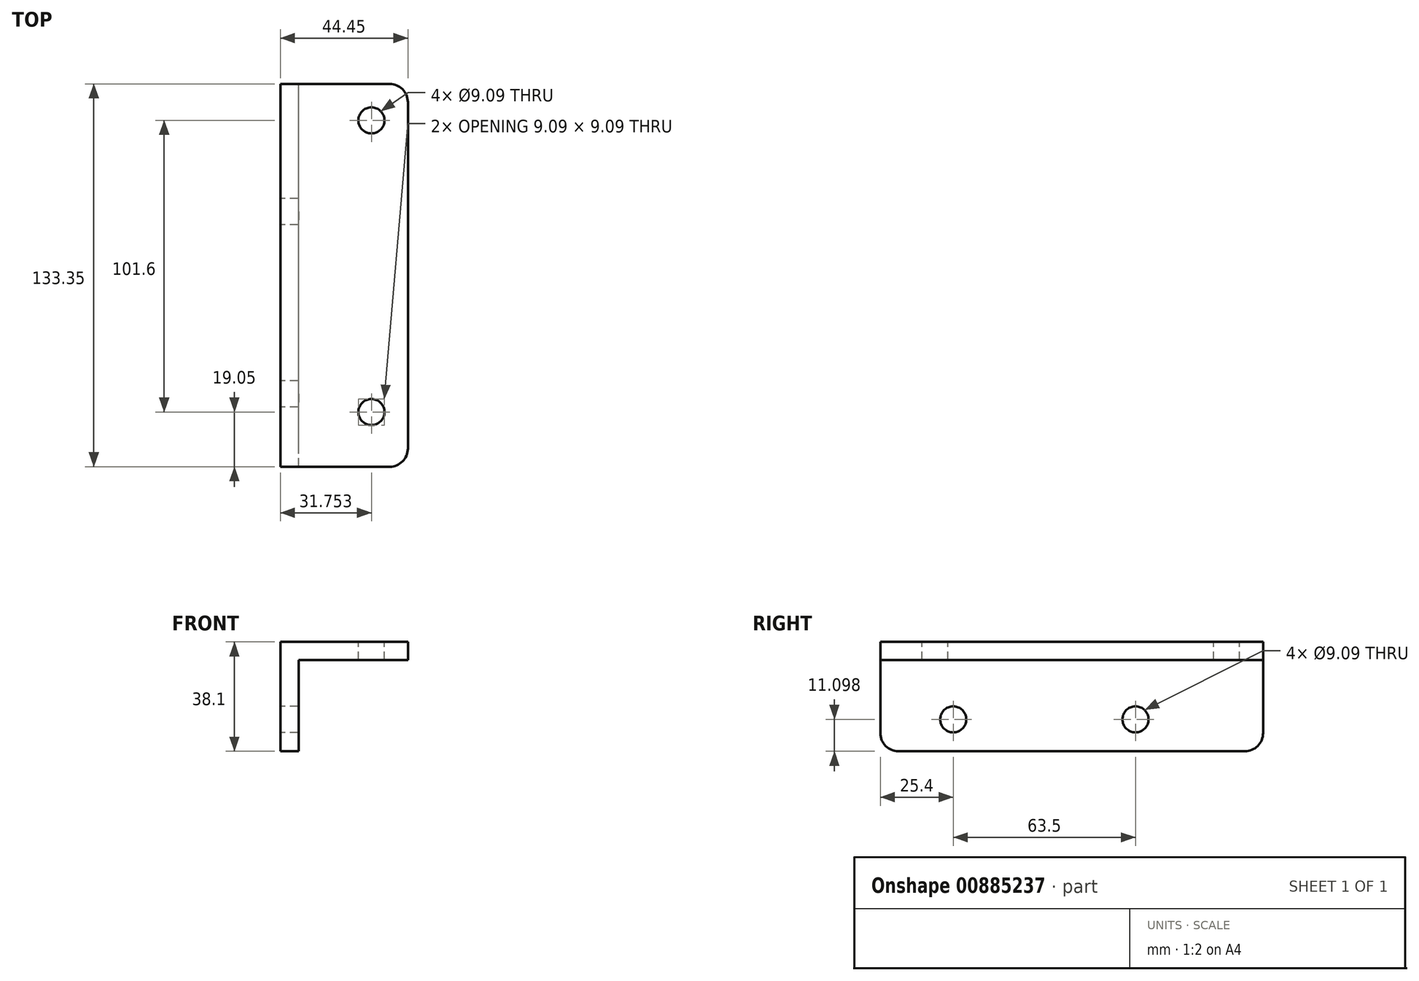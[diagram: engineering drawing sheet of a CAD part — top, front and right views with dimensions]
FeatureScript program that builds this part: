
annotation { "Feature Type Name" : "Feature", "Feature Type Description" : "" }
export const myFeature = defineFeature(function(context is Context, id is Id, definition is map)
    precondition{}
    {
        {
            var Q0;
            Q0=qCreatedBy(makeId("Front.planeOp"),FACE);
            var sketch = newSketch(context, id + "F0", { "sketchPlane" : qUnion([Q0])});
            skLineSegment(sketch, "E0", {"start": v(-40.8, -11.58) * mm, "end": v(-40.8, 26.52) * mm});
            skLineSegment(sketch, "E1", {"start": v(-40.8, 26.52) * mm, "end": v(3.65, 26.52) * mm});
            skLineSegment(sketch, "E2", {"start": v(3.65, 26.52) * mm, "end": v(3.65, 20.17) * mm});
            skLineSegment(sketch, "E3", {"start": v(3.65, 20.17) * mm, "end": v(-34.45, 20.17) * mm});
            skLineSegment(sketch, "E4", {"start": v(-34.45, 20.17) * mm, "end": v(-34.45, -11.58) * mm});
            skLineSegment(sketch, "E5", {"start": v(-34.45, -11.58) * mm, "end": v(-40.8, -11.58) * mm});
            skSolve(sketch);
        }
        {
            var Q0;
            Q0=makeQuery(id+"F0.imprint","IMPRINT",FACE,{"disambiguationData":[TD([[makeQuery(id+"F0.imprint","IMPRINT",EDGE,{"derivedFrom":sQuery(id+"F0.wireOp",EDGE,"E0")}),-1.0]])]});
            extrude(context, id + "F1", {"entities" : qUnion([Q0]), "depth" : 133.35 * mm, "offsetDistance" : 25.4 * mm});
        }
        {
            var Q0;
            Q0=makeQuery(id+"F1.opExtrude","SWEPT_FACE",FACE,{"disambiguationData":[OSD([sQuery(id+"F0.wireOp",EDGE,"E0")])]});
            var sketch = newSketch(context, id + "F2", { "sketchPlane" : qUnion([Q0])});
            skLineSegment(sketch, "E6", {"start": v(133.35, 26.52) * mm, "end": v(133.35, -0.48) * mm, "construction": true});
            skLineSegment(sketch, "E7", {"start": v(133.35, -0.48) * mm, "end": v(107.95, -0.48) * mm, "construction": true});
            skLineSegment(sketch, "E8", {"start": v(107.95, -0.48) * mm, "end": v(44.45, -0.48) * mm, "construction": true});
            skCircle(sketch, "E9", {"center": v(107.95, -0.48) * mm, "radius": 4.55 * mm});
            skCircle(sketch, "E10", {"center": v(44.45, -0.48) * mm, "radius": 4.55 * mm});
            skSolve(sketch);
        }
        {
            var Q0;
            Q0=makeQuery(id+"F2.imprint","IMPRINT",FACE,{"disambiguationData":[TD([[makeQuery(id+"F2.imprint","IMPRINT",EDGE,{"derivedFrom":sQuery(id+"F2.wireOp",EDGE,"E9")}),1.0]])]});
            var Q1;
            Q1=makeQuery(id+"F2.imprint","IMPRINT",FACE,{"disambiguationData":[TD([[makeQuery(id+"F2.imprint","IMPRINT",EDGE,{"derivedFrom":sQuery(id+"F2.wireOp",EDGE,"E10")}),1.0]])]});
            extrude(context, id + "F3", {"entities" : qUnion([Q0, Q1]), "operationType" : NewBodyOperationType.REMOVE, "oppositeDirection" : true, "depth" : 25.4 * mm, "offsetDistance" : 25.4 * mm});
        }
        {
            var Q0;
            Q0=makeQuery(id+"F1.opExtrude","SWEPT_FACE",FACE,{"disambiguationData":[OSD([sQuery(id+"F0.wireOp",EDGE,"E1")])]});
            var sketch = newSketch(context, id + "F4", { "sketchPlane" : qUnion([Q0])});
            skLineSegment(sketch, "E11", {"start": v(3.65, -133.35) * mm, "end": v(-9.05, -133.35) * mm, "construction": true});
            skLineSegment(sketch, "E12", {"start": v(-9.05, -133.35) * mm, "end": v(-9.05, -114.3) * mm, "construction": true});
            skLineSegment(sketch, "E13", {"start": v(-9.05, -114.3) * mm, "end": v(-9.05, -12.7) * mm, "construction": true});
            skCircle(sketch, "E14", {"center": v(-9.05, -12.7) * mm, "radius": 4.55 * mm});
            skCircle(sketch, "E15", {"center": v(-9.05, -114.3) * mm, "radius": 4.55 * mm});
            skSolve(sketch);
        }
        {
            var Q0;
            Q0=makeQuery(id+"F4.imprint","IMPRINT",FACE,{"disambiguationData":[TD([[makeQuery(id+"F4.imprint","IMPRINT",EDGE,{"derivedFrom":sQuery(id+"F4.wireOp",EDGE,"E14")}),1.0]])]});
            var Q1;
            Q1=makeQuery(id+"F4.imprint","IMPRINT",FACE,{"disambiguationData":[TD([[makeQuery(id+"F4.imprint","IMPRINT",EDGE,{"derivedFrom":sQuery(id+"F4.wireOp",EDGE,"E15")}),1.0]])]});
            extrude(context, id + "F5", {"entities" : qUnion([Q0, Q1]), "operationType" : NewBodyOperationType.REMOVE, "oppositeDirection" : true, "depth" : 25.4 * mm, "offsetDistance" : 25.4 * mm});
        }
        {
            var Q0;
            Q0=makeQuery(id+"F1.opExtrude","CAP_EDGE",EDGE,{"disambiguationData":[OSD([sQuery(id+"F0.wireOp",EDGE,"E2")])],"isStart":true});
            var Q1;
            Q1=makeQuery(id+"F1.opExtrude","CAP_EDGE",EDGE,{"disambiguationData":[OSD([sQuery(id+"F0.wireOp",EDGE,"E5")])],"isStart":true});
            var Q2;
            Q2=makeQuery(id+"F1.opExtrude","CAP_EDGE",EDGE,{"disambiguationData":[OSD([sQuery(id+"F0.wireOp",EDGE,"E2")])],"isStart":false});
            var Q3;
            Q3=makeQuery(id+"F1.opExtrude","CAP_EDGE",EDGE,{"disambiguationData":[OSD([sQuery(id+"F0.wireOp",EDGE,"E5")])],"isStart":false});
            fillet(context, id + "F6", {"entities" : qUnion([Q0, Q1, Q2, Q3]), "radius" : 6.35 * mm, "tangentPropagation" : true, "allowEdgeOverflow" : false});
        }
    });
